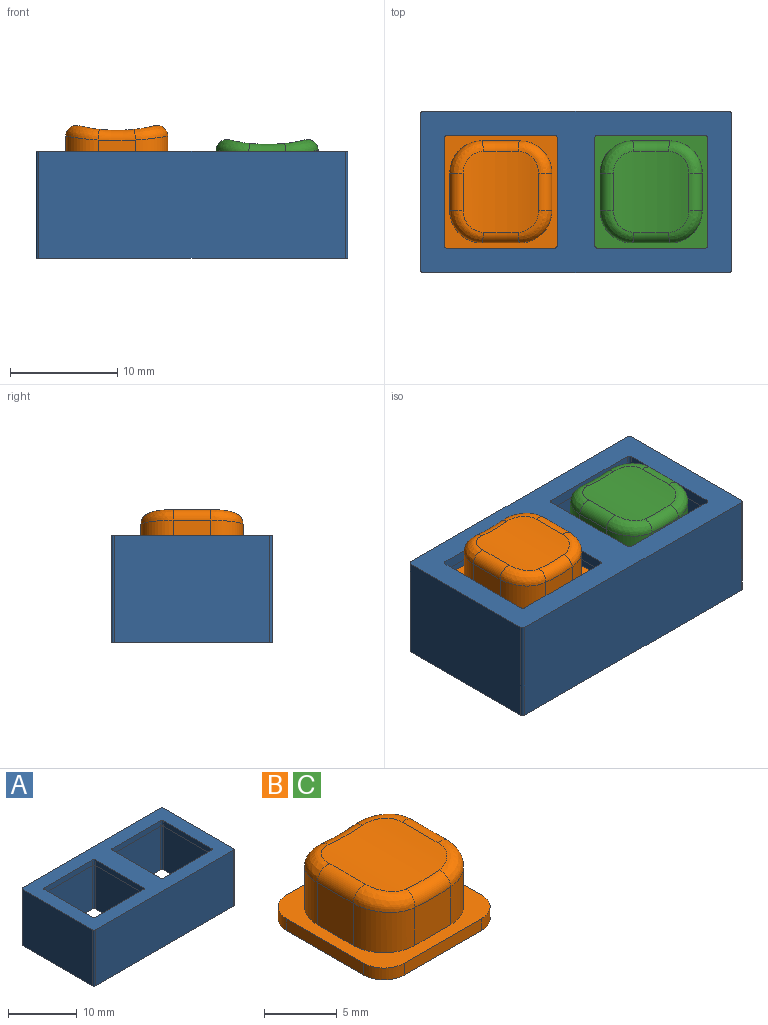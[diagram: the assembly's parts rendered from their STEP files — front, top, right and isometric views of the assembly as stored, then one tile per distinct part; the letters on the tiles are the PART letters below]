
ASSEMBLY  parts=3 mates=2
PART A: 44 faces, bbox 29x15x10 mm
  f0: plane 12.5x9mm, normal (1,0,0), area 112.5mm2, adj f12,f23,f40,f43
  f1: plane 12.5x9mm, normal (0,-1,0), area 112.5mm2, adj f12,f23,f40,f41
  f2: plane 12.5x9mm, normal (-1,0,0), area 112.5mm2, adj f12,f23,f41,f42
  f3: plane 14.5x10mm, normal (-1,0,0), area 145mm2, adj f12,f22,f36,f39
  f4: plane 28.5x10mm, normal (0,-1,0), area 285mm2, adj f12,f22,f36,f37
  f5: plane 14.5x10mm, normal (1,0,0), area 145mm2, adj f12,f22,f37,f38
  f6: plane 12.5x9mm, normal (-1,0,0), area 112.5mm2, adj f12,f13,f32,f35
  f7: plane 12.5x9mm, normal (0,1,0), area 112.5mm2, adj f12,f13,f32,f33
  f8: plane 12.5x9mm, normal (1,0,0), area 112.5mm2, adj f12,f13,f33,f34
  f9: plane 28.5x10mm, normal (0,1,0), area 285mm2, adj f12,f22,f38,f39
  f10: plane 12.5x9mm, normal (0,-1,0), area 112.5mm2, adj f12,f13,f34,f35
  f11: plane 12.5x9mm, normal (0,1,0), area 112.5mm2, adj f12,f23,f42,f43
  f12: plane 29x15mm, normal (0,0,-1), area 97.1mm2, adj f0,f1,f2,f3,f4,f5,f6,f7
  f13: plane 13x13mm, normal (0,0,-1), area 58.8mm2, adj f6,f7,f8,f10,f17,f18,f19,f20
  f14: plane 10x1mm, normal (1,0,0), area 10mm2, adj f22,f23,f28,f31
  f15: plane 10x1mm, normal (0,-1,0), area 10mm2, adj f22,f23,f28,f29
  f16: plane 10x1mm, normal (-1,0,0), area 10mm2, adj f22,f23,f29,f30
  f17: plane 10x1mm, normal (1,0,0), area 10mm2, adj f13,f22,f24,f27
  f18: plane 10x1mm, normal (0,-1,0), area 10mm2, adj f13,f22,f24,f25
  f19: plane 10x1mm, normal (-1,0,0), area 10mm2, adj f13,f22,f25,f26
  f20: plane 10x1mm, normal (0,1,0), area 10mm2, adj f13,f22,f26,f27
  f21: plane 10x1mm, normal (0,1,0), area 10mm2, adj f22,f23,f30,f31
  f22: plane 29x15mm, normal (0,0,1), area 214.6mm2, adj f3,f4,f5,f9,f14,f15,f16,f17
  f23: plane 13x13mm, normal (0,0,-1), area 58.8mm2, adj f0,f1,f2,f11,f14,f15,f16,f21
  f24: cylinder r=0.25mm len=1mm, axis (0,0,-1), area 0.4mm2, adj f13,f17,f18,f22
  f25: cylinder r=0.25mm len=1mm, axis (0,0,1), area 0.4mm2, adj f13,f18,f19,f22
  f26: cylinder r=0.25mm len=1mm, axis (0,0,-1), area 0.4mm2, adj f13,f19,f20,f22
  f27: cylinder r=0.25mm len=1mm, axis (0,0,1), area 0.4mm2, adj f13,f17,f20,f22
  f28: cylinder r=0.25mm len=1mm, axis (0,0,-1), area 0.4mm2, adj f14,f15,f22,f23
  f29: cylinder r=0.25mm len=1mm, axis (0,0,1), area 0.4mm2, adj f15,f16,f22,f23
  f30: cylinder r=0.25mm len=1mm, axis (0,0,-1), area 0.4mm2, adj f16,f21,f22,f23
  f31: cylinder r=0.25mm len=1mm, axis (0,0,1), area 0.4mm2, adj f14,f21,f22,f23
  f32: cylinder r=0.25mm len=9mm, axis (0,0,-1), area 3.5mm2, adj f6,f7,f12,f13
  f33: cylinder r=0.25mm len=9mm, axis (0,0,1), area 3.5mm2, adj f7,f8,f12,f13
  f34: cylinder r=0.25mm len=9mm, axis (0,0,-1), area 3.5mm2, adj f8,f10,f12,f13
  f35: cylinder r=0.25mm len=9mm, axis (0,0,1), area 3.5mm2, adj f6,f10,f12,f13
  f36: cylinder r=0.25mm len=10mm, axis (0,0,-1), area 3.9mm2, adj f3,f4,f12,f22
  f37: cylinder r=0.25mm len=10mm, axis (0,0,-1), area 3.9mm2, adj f4,f5,f12,f22
  f38: cylinder r=0.25mm len=10mm, axis (0,0,-1), area 3.9mm2, adj f5,f9,f12,f22
  f39: cylinder r=0.25mm len=10mm, axis (0,0,-1), area 3.9mm2, adj f3,f9,f12,f22
  f40: cylinder r=0.25mm len=9mm, axis (0,0,-1), area 3.5mm2, adj f0,f1,f12,f23
  f41: cylinder r=0.25mm len=9mm, axis (0,0,1), area 3.5mm2, adj f1,f2,f12,f23
  f42: cylinder r=0.25mm len=9mm, axis (0,0,-1), area 3.5mm2, adj f2,f11,f12,f23
  f43: cylinder r=0.25mm len=9mm, axis (0,0,1), area 3.5mm2, adj f0,f11,f12,f23
PART B: 27 faces, bbox 11.5x11.5x5.8 mm
  f0: plane 11.5x11.5mm, normal (0,0,1), area 46.3mm2, adj f1,f2,f3,f4,f6,f7,f8,f9
  f1: plane 7.5x1mm, normal (0,1,0), area 7.5mm2, adj f0,f5,f23,f26
  f2: plane 7.5x1mm, normal (-1,0,0), area 7.5mm2, adj f0,f5,f23,f24
  f3: plane 7.5x1mm, normal (0,-1,0), area 7.5mm2, adj f0,f5,f24,f25
  f4: plane 7.5x1mm, normal (1,0,0), area 7.5mm2, adj f0,f5,f25,f26
  f5: plane 11.5x11.5mm, normal (0,0,-1), area 128.8mm2, adj f1,f2,f3,f4,f23,f24,f25,f26
  f6: plane 3.5x3.2mm, normal (0,1,0), area 11mm2, adj f0,f11,f14,f19
  f7: plane 3.55x3.5mm, normal (-1,0,0), area 12.4mm2, adj f0,f11,f12,f15
  f8: plane 3.5x3.2mm, normal (0,-1,0), area 11mm2, adj f0,f12,f13,f18
  f9: plane 3.55x3.5mm, normal (1,0,0), area 12.4mm2, adj f0,f13,f14,f22
  f10: cylinder r=15mm len=7.5mm, axis (0,1,0), area 49.9mm2, adj f15,f16,f17,f18,f19,f20,f21,f22
  f11: cylinder r=3mm len=3.55mm, axis (0,0,1), area 16mm2, adj f0,f6,f7,f17
  f12: cylinder r=3mm len=3.55mm, axis (0,0,-1), area 16mm2, adj f0,f7,f8,f16
  f13: cylinder r=3mm len=3.55mm, axis (0,0,1), area 16mm2, adj f0,f8,f9,f20
  f14: cylinder r=3mm len=3.55mm, axis (0,0,-1), area 16mm2, adj f0,f6,f9,f21
  f15: cylinder r=1mm len=3.5mm, axis (0,1,0), area 6.3mm2, adj f7,f10,f16,f17
  f16: bspline ~3.74x3.73mm, area 7.1mm2, adj f10,f12,f15,f18
  f17: bspline ~3.74x3.73mm, area 7.1mm2, adj f10,f11,f15,f19
  f18: torus R=16mm, axis (0,1,0), area 5.3mm2, adj f8,f10,f16,f20
  f19: torus R=16mm, axis (0,1,0), area 5.3mm2, adj f6,f10,f17,f21
  f20: bspline ~3.74x3.73mm, area 7.1mm2, adj f10,f13,f18,f22
  f21: bspline ~3.74x3.73mm, area 7.1mm2, adj f10,f14,f19,f22
  f22: cylinder r=1mm len=3.5mm, axis (0,1,0), area 6.3mm2, adj f9,f10,f20,f21
  f23: cylinder r=2mm len=2mm, axis (0,0,1), area 3.1mm2, adj f0,f1,f2,f5
  f24: cylinder r=2mm len=2mm, axis (0,0,-1), area 3.1mm2, adj f0,f2,f3,f5
  f25: cylinder r=2mm len=2mm, axis (0,0,1), area 3.1mm2, adj f0,f3,f4,f5
  f26: cylinder r=2mm len=2mm, axis (0,0,-1), area 3.1mm2, adj f0,f1,f4,f5
PART C: same geometry as B
PLACE A t=(-7,0,0)mm
PLACE B t=(-7,0,6.83)mm
PLACE C t=(7,0,5.52)mm
MATE slider B.f5 <-> A.f22  axis (0,0,-1) through (-7,0,6.83)mm
MATE slider A.f22 <-> C.f5  axis (0,0,1) through (7,0,10)mm
